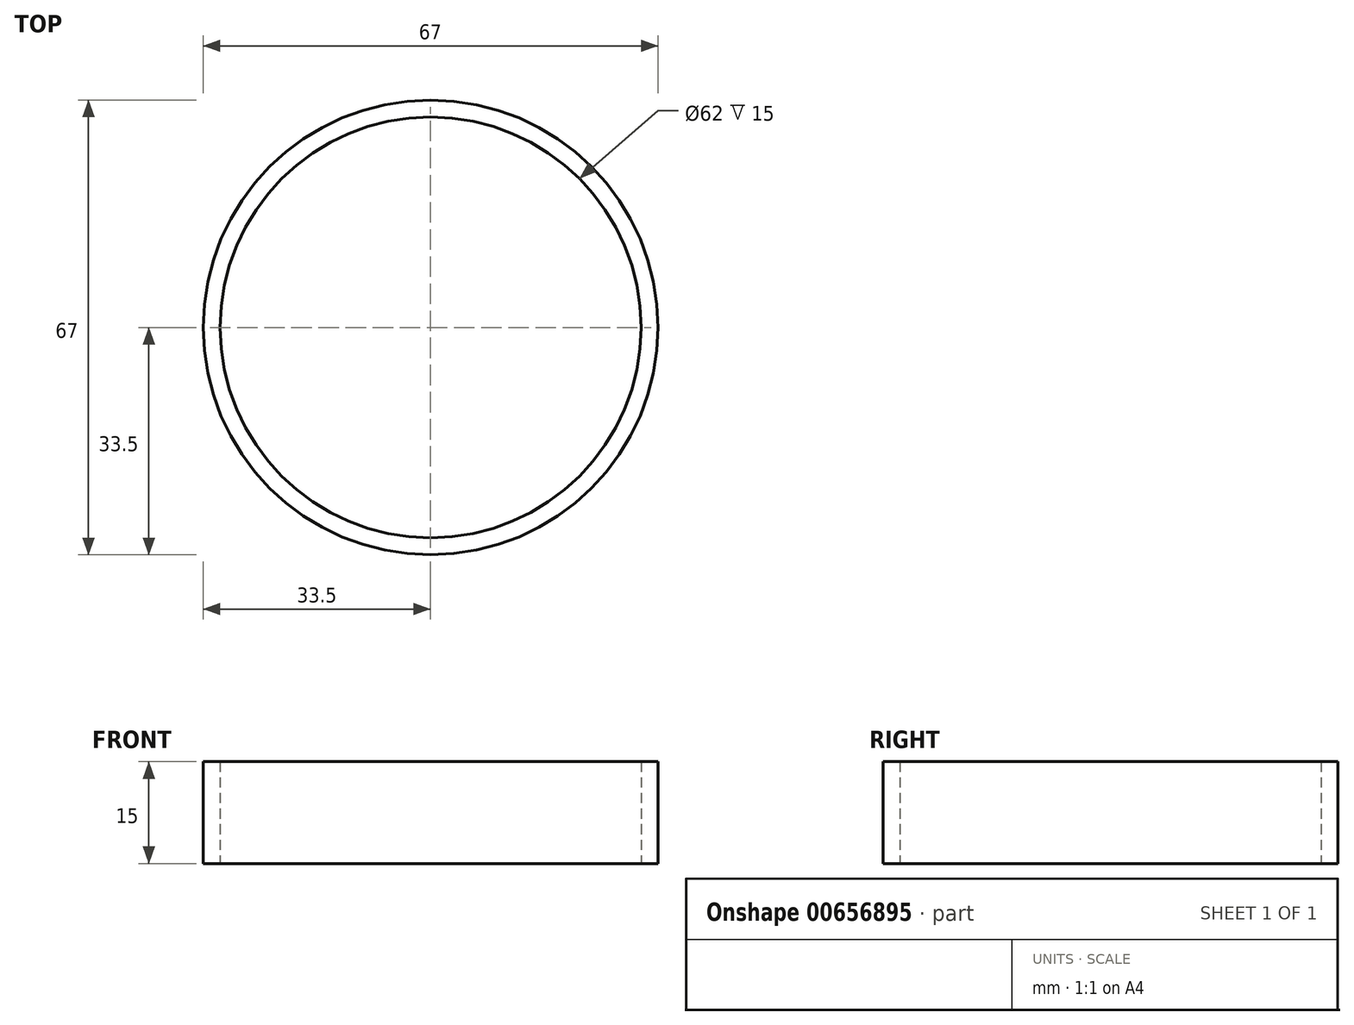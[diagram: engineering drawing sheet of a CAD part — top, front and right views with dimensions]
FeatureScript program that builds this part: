
annotation { "Feature Type Name" : "Feature", "Feature Type Description" : "" }
export const myFeature = defineFeature(function(context is Context, id is Id, definition is map)
    precondition{}
    {
        {
            var Q0;
            Q0=qCreatedBy(makeId("Top.planeOp"),FACE);
            var sketch = newSketch(context, id + "F0", { "sketchPlane" : qUnion([Q0])});
            skCircle(sketch, "E0", {"center": v(0, 0) * mm, "radius": 33.5 * mm});
            skCircle(sketch, "E1", {"center": v(0, 0) * mm, "radius": 31 * mm});
            skSolve(sketch);
        }
        {
            var Q0;
            Q0=makeQuery(id+"F0.imprint","IMPRINT",FACE,{"disambiguationData":[TD([[makeQuery(id+"F0.imprint","IMPRINT",EDGE,{"derivedFrom":sQuery(id+"F0.wireOp",EDGE,"E0")}),1.0]])]});
            extrude(context, id + "F1", {"entities" : qUnion([Q0]), "depth" : 15 * mm, "offsetDistance" : 25 * mm});
        }
    });
